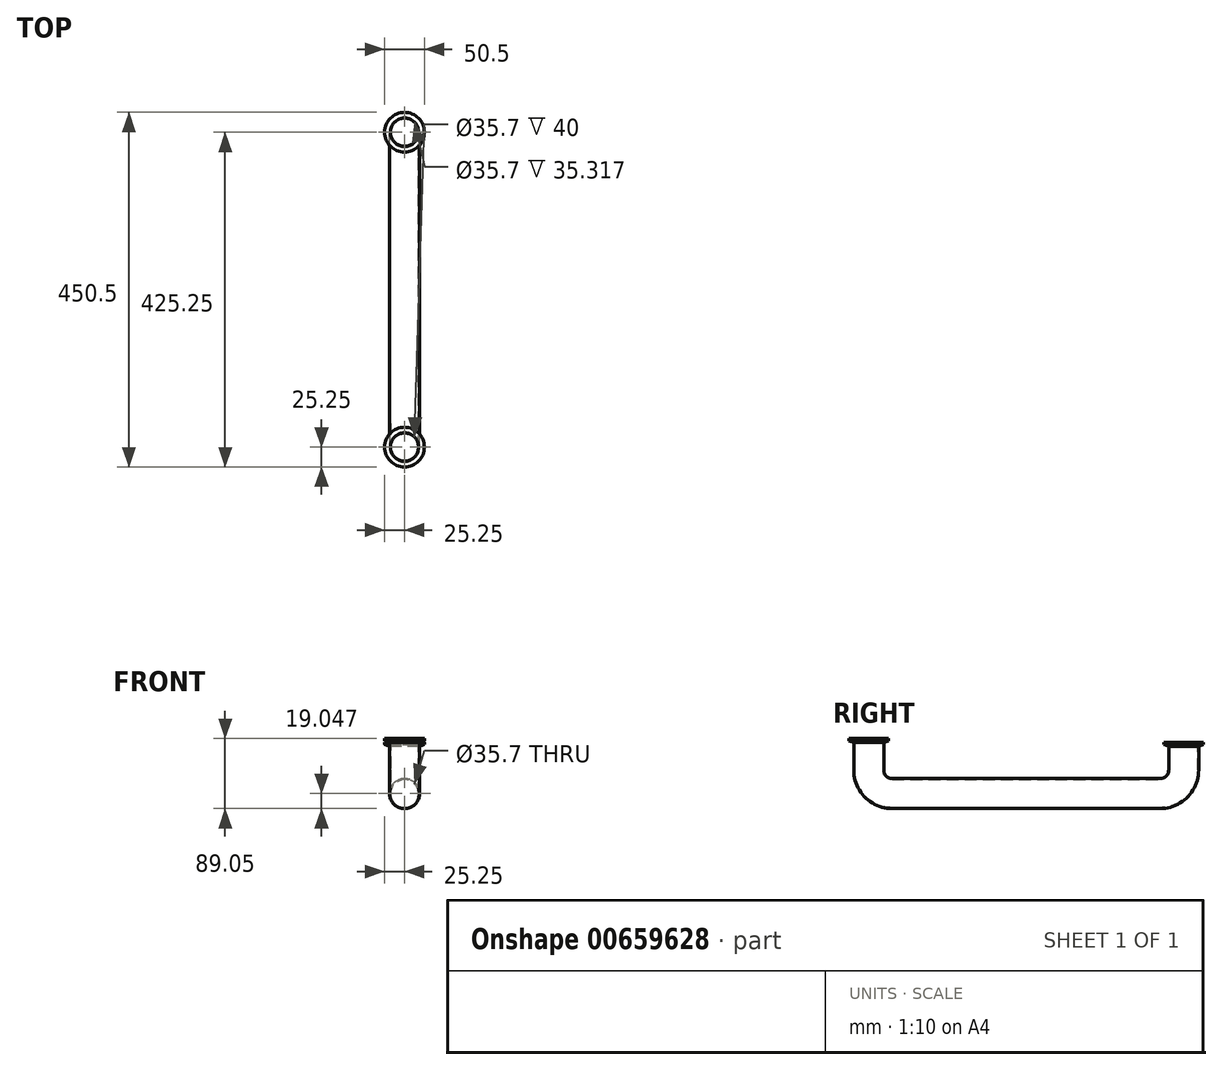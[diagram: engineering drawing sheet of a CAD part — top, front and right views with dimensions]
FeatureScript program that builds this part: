
annotation { "Feature Type Name" : "Feature", "Feature Type Description" : "" }
export const myFeature = defineFeature(function(context is Context, id is Id, definition is map)
    precondition{}
    {
        {
            var Q0;
            Q0=qCreatedBy(makeId("Front.planeOp"),FACE);
            var sketch = newSketch(context, id + "F0", { "sketchPlane" : qUnion([Q0])});
            skLineSegment(sketch, "E0", {"start": v(17.85, 0) * mm, "end": v(17.85, 5.1) * mm});
            skLineSegment(sketch, "E1", {"start": v(17.85, 5.1) * mm, "end": v(25.25, 5.1) * mm});
            skLineSegment(sketch, "E2", {"start": v(25.25, 5.1) * mm, "end": v(25.25, 2.26) * mm});
            skLineSegment(sketch, "E3", {"start": v(25.25, 2.26) * mm, "end": v(19.05, 0) * mm});
            skLineSegment(sketch, "E4", {"start": v(19.05, 0) * mm, "end": v(17.85, 0) * mm});
            skLineSegment(sketch, "E5", {"start": v(0, 0) * mm, "end": v(0, 11.29) * mm, "construction": true});
            skSolve(sketch);
        }
        {
            var Q0;
            Q0=qSketchRegion(id+"F0",true);
            var Q1;
            Q1=sQuery(id+"F0.wireOp",EDGE,"E5");
            revolve(context, id + "F1", {"entities" : qUnion([Q0]), "axis" : qUnion([Q1]), "revolveType" : RevolveType.FULL});
        }
        {
            var Q0;
            Q0=qCreatedBy(makeId("Top.planeOp"),FACE);
            var sketch = newSketch(context, id + "F2", { "sketchPlane" : qUnion([Q0])});
            skCircle(sketch, "E6", {"center": v(0, 0) * mm, "radius": 19.05 * mm});
            skCircle(sketch, "E7", {"center": v(0, 0) * mm, "radius": 17.85 * mm});
            skSolve(sketch);
        }
        {
            var Q0;
            Q0=qCreatedBy(makeId("Right.planeOp"),FACE);
            var sketch = newSketch(context, id + "F3", { "sketchPlane" : qUnion([Q0])});
            skLineSegment(sketch, "E8", {"start": v(0, 0) * mm, "end": v(0, -34.9) * mm});
            skLineSegment(sketch, "E9", {"start": v(30, -64.9) * mm, "end": v(370, -64.9) * mm});
            skPoint(sketch, "E10.visualSharp", {"position": v(0, -64.9) * mm});
            skArc(sketch, "E10.filletArc", {"start": v(0, -34.9) * mm, "mid": v(8.79, -56.1) * mm, "end": v(30, -64.9) * mm});
            skLineSegment(sketch, "E11", {"start": v(400, -34.9) * mm, "end": v(400, -4.68) * mm});
            skPoint(sketch, "E12.visualSharp", {"position": v(400, -64.9) * mm});
            skArc(sketch, "E12.filletArc", {"start": v(370, -64.9) * mm, "mid": v(391.21, -56.1) * mm, "end": v(400, -34.9) * mm});
            skSolve(sketch);
        }
        {
            var Q0;
            Q0=qSketchRegion(id+"F2",true);
            var Q1;
            Q1=qConstructionFilter(qBodyType(qCreatedBy(id+"F3",EDGE),BodyType.WIRE),ConstructionObject.NO);
            sweep(context, id + "F4", {"operationType" : NewBodyOperationType.ADD, "profiles" : qUnion([Q0]), "path" : qUnion([Q1])});
        }
        {
            var Q0;
            Q0=qCreatedBy(makeId("Right.planeOp"),FACE);
            var sketch = newSketch(context, id + "F5", { "sketchPlane" : qUnion([Q0])});
            skLineSegment(sketch, "E13", {"start": v(417.85, -4.68) * mm, "end": v(417.85, 0.42) * mm});
            skLineSegment(sketch, "E14", {"start": v(417.85, 0.42) * mm, "end": v(425.25, 0.42) * mm});
            skLineSegment(sketch, "E15", {"start": v(425.25, 0.42) * mm, "end": v(425.25, -2.43) * mm});
            skLineSegment(sketch, "E16", {"start": v(425.25, -2.43) * mm, "end": v(419.05, -4.68) * mm});
            skLineSegment(sketch, "E17", {"start": v(419.05, -4.68) * mm, "end": v(417.85, -4.68) * mm});
            skSolve(sketch);
        }
        {
            var Q0;
            Q0=qSketchRegion(id+"F5",true);
            var Q1;
            Q1=sQuery(id+"F3.wireOp",EDGE,"E11");
            revolve(context, id + "F6", {"operationType" : NewBodyOperationType.ADD, "entities" : qUnion([Q0]), "axis" : qUnion([Q1]), "revolveType" : RevolveType.FULL});
        }
    });
